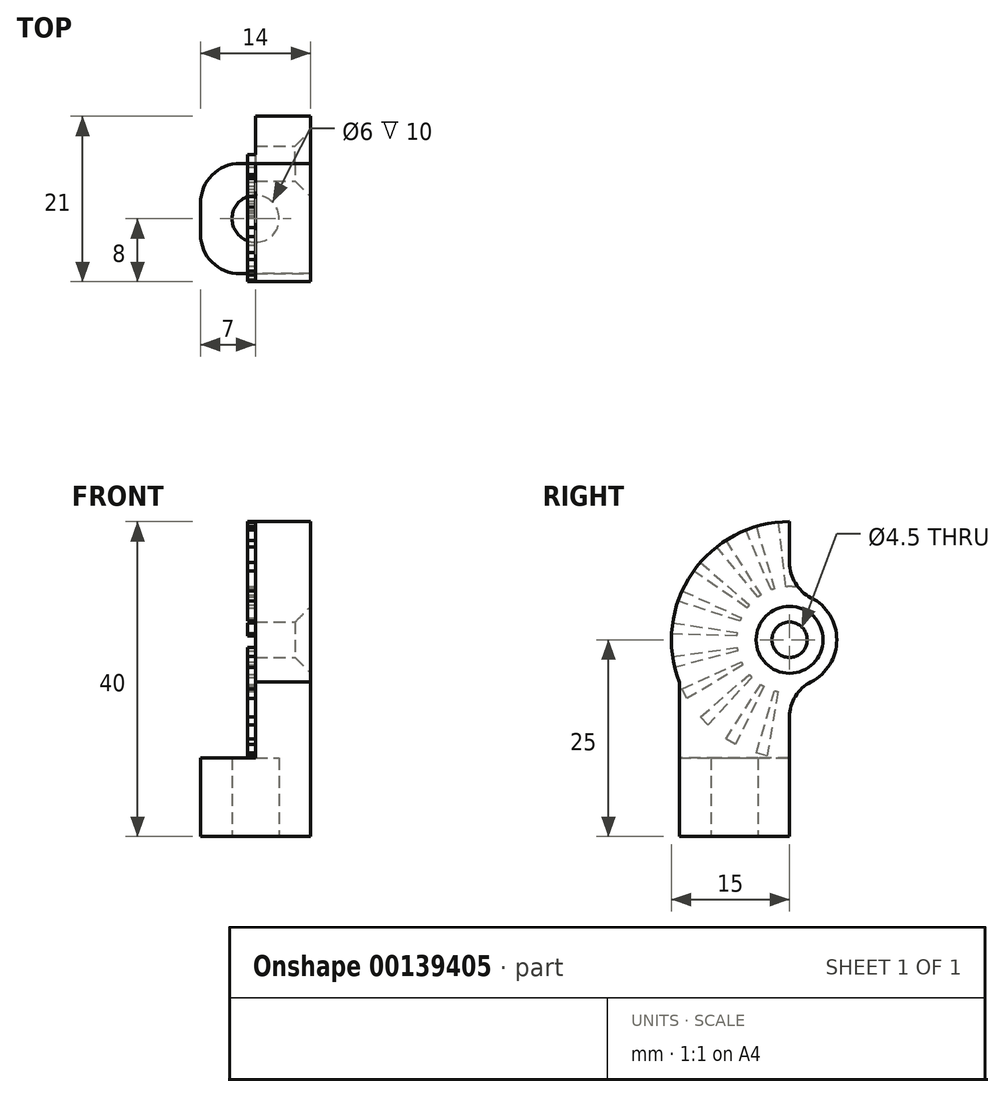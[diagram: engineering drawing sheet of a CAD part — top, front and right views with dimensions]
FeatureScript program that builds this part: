
annotation { "Feature Type Name" : "Feature", "Feature Type Description" : "" }
export const myFeature = defineFeature(function(context is Context, id is Id, definition is map)
    precondition{}
    {
        {
            var Q0;
            Q0=qCreatedBy(makeId("Top.planeOp"),FACE);
            var sketch = newSketch(context, id + "F0", { "sketchPlane" : qUnion([Q0])});
            skLineSegment(sketch, "E0.bottom", {"start": v(7, -7) * mm, "end": v(-7, -7) * mm});
            skLineSegment(sketch, "E0.top", {"start": v(7, 7) * mm, "end": v(-7, 7) * mm});
            skLineSegment(sketch, "E0.left", {"start": v(7, -7) * mm, "end": v(7, 7) * mm});
            skLineSegment(sketch, "E0.right", {"start": v(-7, -7) * mm, "end": v(-7, 7) * mm});
            skPoint(sketch, "E0.middle", {"position": v(0, 0) * mm});
            skCircle(sketch, "E1", {"center": v(0, 0) * mm, "radius": 3 * mm});
            skSolve(sketch);
        }
        {
            var Q0;
            Q0 = qSketchRegion(id + "F0", true);
            var Q1;
            Q1=makeQuery(id+"F0.imprint","IMPRINT",FACE,{"disambiguationData":[TD([[makeQuery(id+"F0.imprint","IMPRINT",EDGE,{"derivedFrom":sQuery(id+"F0.wireOp",EDGE,"E0.bottom")}),-1.0]])]});
            extrude(context, id + "F1", {"entities" : qUnion([Q0, Q1]), "depth" : 10 * mm});
        }
        {
            var Q0;
            Q0=makeQuery(id+"F1.opExtrude","SWEPT_FACE",FACE,{"disambiguationData":[OSD([sQuery(id+"F0.wireOp",EDGE,"E0.left")])]});
            var sketch = newSketch(context, id + "F2", { "sketchPlane" : qUnion([Q0])});
            skPoint(sketch, "E2.centerSnap0", {"position": v(0, 10) * mm});
            skLineSegment(sketch, "E3", {"start": v(7, 10) * mm, "end": v(7, 22.75) * mm, "construction": true});
            skArc(sketch, "E4", {"start": v(7, 40) * mm, "mid": v(-8, 25) * mm, "end": v(7, 10) * mm});
            skLineSegment(sketch, "E5", {"start": v(-7, 10) * mm, "end": v(-7, 19.61) * mm});
            skLineSegment(sketch, "E6", {"start": v(7, 40) * mm, "end": v(7, 27.25) * mm});
            skArc(sketch, "E7", {"start": v(7, 19) * mm, "mid": v(13, 25) * mm, "end": v(7, 31) * mm});
            skCircle(sketch, "E8", {"center": v(7, 25) * mm, "radius": 2.25 * mm});
            skLineSegment(sketch, "E9.trimOffspring", {"start": v(7, 27.25) * mm, "end": v(7, 46.14) * mm, "construction": true});
            skLineSegment(sketch, "E10.trimOffspring", {"start": v(7, 22.75) * mm, "end": v(7, 10) * mm});
            skSolve(sketch);
        }
        {
            var Q0;
            Q0 = qSketchRegion(id + "F2", true);
            var Q1;
            {var subQ1=sQuery(id+"F2.wireOp",EDGE,"E6");var subQ5=sQuery(id+"F2.wireOp",EDGE,"E4");var subQ6=makeQuery(id+"F2.imprint","INTERSECT",VERTEX,{"derivedFrom":[subQ5,subQ1]});Q1=makeQuery(id+"F2.imprint","IMPRINT",FACE,{"disambiguationData":[TD([[makeQuery(id+"F2.imprint","IMPRINT",EDGE,{"disambiguationData":[TD([[subQ6,-1.0]])],"derivedFrom":subQ5}),1.0]])]});}
            var Q2;
            {var subQ3=sQuery(id+"F2.wireOp",EDGE,"E5");Q2=makeQuery(id+"F2.imprint","IMPRINT",FACE,{"disambiguationData":[TD([[makeQuery(id+"F2.imprint","IMPRINT",EDGE,{"derivedFrom":subQ3}),-1.0]])]});}
            extrude(context, id + "F3", {"entities" : qUnion([Q0, Q1, Q2]), "operationType" : NewBodyOperationType.ADD, "oppositeDirection" : true, "depth" : 7 * mm});
        }
        {
            var Q0;
            Q0=makeQuery(id+"F3.opExtrude","CAP_FACE",FACE,{"disambiguationData":[OSD([sQuery(id+"F0.wireOp",EDGE,"E0.left"),sQuery(id+"F2.wireOp",EDGE,"E4"),sQuery(id+"F2.wireOp",EDGE,"E5"),sQuery(id+"F2.wireOp",EDGE,"E6"),sQuery(id+"F2.wireOp",EDGE,"E7"),sQuery(id+"F2.wireOp",EDGE,"E8"),sQuery(id+"F2.wireOp",EDGE,"E10.trimOffspring")])],"isStart":false});
            var sketch = newSketch(context, id + "F4", { "sketchPlane" : qUnion([Q0])});
            skPoint(sketch, "E11.center", {"position": v(0, 0) * mm});
            skArc(sketch, "E12", {"start": v(-7, 18.25) * mm, "mid": v(-0.25, 25) * mm, "end": v(-7, 31.75) * mm, "construction": true});
            skLineSegment(sketch, "E13", {"start": v(-7, 40) * mm, "end": v(-7, 31.75) * mm});
            skLineSegment(sketch, "E14", {"start": v(-7, 31.75) * mm, "end": v(-6.55, 31.73) * mm});
            skLineSegment(sketch, "E15", {"start": v(-6.55, 31.73) * mm, "end": v(-5.6, 39.93) * mm});
            skLineSegment(sketch, "E16", {"start": v(-5.6, 39.93) * mm, "end": v(-7, 40) * mm});
            skLineSegment(sketch, "E17.1.0", {"start": v(-1.45, 38.94) * mm, "end": v(-2.77, 39.4) * mm});
            skLineSegment(sketch, "E17.1.1", {"start": v(-2.77, 39.4) * mm, "end": v(-5.1, 31.48) * mm});
            skLineSegment(sketch, "E17.1.2", {"start": v(-5.1, 31.48) * mm, "end": v(-4.67, 31.34) * mm});
            skLineSegment(sketch, "E17.1.3", {"start": v(-4.67, 31.34) * mm, "end": v(-1.45, 38.94) * mm});
            skLineSegment(sketch, "E17.2.0", {"start": v(2.25, 36.8) * mm, "end": v(1.1, 37.62) * mm});
            skLineSegment(sketch, "E17.2.1", {"start": v(1.1, 37.62) * mm, "end": v(-3.35, 30.68) * mm});
            skLineSegment(sketch, "E17.2.2", {"start": v(-3.35, 30.68) * mm, "end": v(-2.98, 30.42) * mm});
            skLineSegment(sketch, "E17.2.3", {"start": v(-2.98, 30.42) * mm, "end": v(2.25, 36.8) * mm});
            skLineSegment(sketch, "E17.3.0", {"start": v(5.2, 33.72) * mm, "end": v(4.34, 34.82) * mm});
            skLineSegment(sketch, "E17.3.1", {"start": v(4.34, 34.82) * mm, "end": v(-1.9, 29.42) * mm});
            skLineSegment(sketch, "E17.3.2", {"start": v(-1.9, 29.42) * mm, "end": v(-1.62, 29.07) * mm});
            skLineSegment(sketch, "E17.3.3", {"start": v(-1.62, 29.07) * mm, "end": v(5.2, 33.72) * mm});
            skLineSegment(sketch, "E17.4.0", {"start": v(7.17, 29.93) * mm, "end": v(6.64, 31.23) * mm});
            skLineSegment(sketch, "E17.4.1", {"start": v(6.64, 31.23) * mm, "end": v(-0.86, 27.8) * mm});
            skLineSegment(sketch, "E17.4.2", {"start": v(-0.86, 27.8) * mm, "end": v(-0.69, 27.39) * mm});
            skLineSegment(sketch, "E17.4.3", {"start": v(-0.69, 27.39) * mm, "end": v(7.17, 29.93) * mm});
            skLineSegment(sketch, "E17.5.0", {"start": v(7.98, 25.74) * mm, "end": v(7.85, 27.13) * mm});
            skLineSegment(sketch, "E17.5.1", {"start": v(7.85, 27.13) * mm, "end": v(-0.32, 25.96) * mm});
            skLineSegment(sketch, "E17.5.2", {"start": v(-0.32, 25.96) * mm, "end": v(-0.27, 25.51) * mm});
            skLineSegment(sketch, "E17.5.3", {"start": v(-0.27, 25.51) * mm, "end": v(7.98, 25.74) * mm});
            skLineSegment(sketch, "E17.6.0", {"start": v(7.58, 21.5) * mm, "end": v(7.85, 22.87) * mm});
            skLineSegment(sketch, "E17.6.1", {"start": v(7.85, 22.87) * mm, "end": v(-0.32, 24.04) * mm});
            skLineSegment(sketch, "E17.6.2", {"start": v(-0.32, 24.04) * mm, "end": v(-0.4, 23.6) * mm});
            skLineSegment(sketch, "E17.6.3", {"start": v(-0.4, 23.6) * mm, "end": v(7.58, 21.5) * mm});
            skLineSegment(sketch, "E17.7.0", {"start": v(6, 17.52) * mm, "end": v(6.64, 18.77) * mm});
            skLineSegment(sketch, "E17.7.1", {"start": v(6.64, 18.77) * mm, "end": v(-0.86, 22.2) * mm});
            skLineSegment(sketch, "E17.7.2", {"start": v(-0.86, 22.2) * mm, "end": v(-1.06, 21.8) * mm});
            skLineSegment(sketch, "E17.7.3", {"start": v(-1.06, 21.8) * mm, "end": v(6, 17.52) * mm});
            skLineSegment(sketch, "E17.8.0", {"start": v(3.37, 14.16) * mm, "end": v(4.34, 15.18) * mm});
            skLineSegment(sketch, "E17.8.1", {"start": v(4.34, 15.18) * mm, "end": v(-1.9, 20.58) * mm});
            skLineSegment(sketch, "E17.8.2", {"start": v(-1.9, 20.58) * mm, "end": v(-2.2, 20.25) * mm});
            skLineSegment(sketch, "E17.8.3", {"start": v(-2.2, 20.25) * mm, "end": v(3.37, 14.16) * mm});
            skLineSegment(sketch, "E17.9.0", {"start": v(-0.1, 11.68) * mm, "end": v(1.1, 12.38) * mm});
            skLineSegment(sketch, "E17.9.1", {"start": v(1.1, 12.38) * mm, "end": v(-3.35, 19.32) * mm});
            skLineSegment(sketch, "E17.9.2", {"start": v(-3.35, 19.32) * mm, "end": v(-3.74, 19.1) * mm});
            skLineSegment(sketch, "E17.9.3", {"start": v(-3.74, 19.1) * mm, "end": v(-0.1, 11.68) * mm});
            skLineSegment(sketch, "E17.10.0", {"start": v(-4.13, 10.28) * mm, "end": v(-2.77, 10.6) * mm});
            skLineSegment(sketch, "E17.10.1", {"start": v(-2.77, 10.6) * mm, "end": v(-5.1, 18.52) * mm});
            skLineSegment(sketch, "E17.10.2", {"start": v(-5.1, 18.52) * mm, "end": v(-5.53, 18.41) * mm});
            skLineSegment(sketch, "E17.10.3", {"start": v(-5.53, 18.41) * mm, "end": v(-4.13, 10.28) * mm});
            skLineSegment(sketch, "E17.11.0", {"start": v(-8.4, 10.07) * mm, "end": v(-7, 10) * mm});
            skLineSegment(sketch, "E17.11.1", {"start": v(-7, 10) * mm, "end": v(-7, 18.25) * mm});
            skLineSegment(sketch, "E17.11.2", {"start": v(-7, 18.25) * mm, "end": v(-7.45, 18.27) * mm});
            skLineSegment(sketch, "E17.11.3", {"start": v(-7.45, 18.27) * mm, "end": v(-8.4, 10.07) * mm});
            skLineSegment(sketch, "E17.anchor1", {"start": v(-7, 25) * mm, "end": v(-7, 40) * mm, "construction": true});
            skLineSegment(sketch, "E17.anchor2", {"start": v(-7, 25) * mm, "end": v(-7, 10) * mm, "construction": true});
            skArc(sketch, "E18", {"start": v(-7, 18.25) * mm, "mid": v(-0.25, 25) * mm, "end": v(-7, 31.75) * mm});
            skSolve(sketch);
        }
        {
            var Q0;
            {var subQ0=sQuery(id+"F4.wireOp",EDGE,"E13");Q0=makeQuery(id+"F4.imprint","IMPRINT",FACE,{"disambiguationData":[TD([[makeQuery(id+"F4.imprint","IMPRINT",EDGE,{"derivedFrom":subQ0}),1.0]])]});}
            var Q1;
            Q1=makeQuery(id+"F4.imprint","IMPRINT",FACE,{"disambiguationData":[TD([[makeQuery(id+"F4.imprint","IMPRINT",EDGE,{"derivedFrom":sQuery(id+"F4.wireOp",EDGE,"E17.1.0")}),1.0]])]});
            var Q2;
            Q2=makeQuery(id+"F4.imprint","IMPRINT",FACE,{"disambiguationData":[TD([[makeQuery(id+"F4.imprint","IMPRINT",EDGE,{"derivedFrom":sQuery(id+"F4.wireOp",EDGE,"E17.2.0")}),1.0]])]});
            var Q3;
            Q3=makeQuery(id+"F4.imprint","IMPRINT",FACE,{"disambiguationData":[TD([[makeQuery(id+"F4.imprint","IMPRINT",EDGE,{"derivedFrom":sQuery(id+"F4.wireOp",EDGE,"E17.3.0")}),1.0]])]});
            var Q4;
            Q4=makeQuery(id+"F4.imprint","IMPRINT",FACE,{"disambiguationData":[TD([[makeQuery(id+"F4.imprint","IMPRINT",EDGE,{"derivedFrom":sQuery(id+"F4.wireOp",EDGE,"E17.4.0")}),1.0]])]});
            var Q5;
            Q5=makeQuery(id+"F4.imprint","IMPRINT",FACE,{"disambiguationData":[TD([[makeQuery(id+"F4.imprint","IMPRINT",EDGE,{"derivedFrom":sQuery(id+"F4.wireOp",EDGE,"E17.5.0")}),1.0]])]});
            var Q6;
            Q6=makeQuery(id+"F4.imprint","IMPRINT",FACE,{"disambiguationData":[TD([[makeQuery(id+"F4.imprint","IMPRINT",EDGE,{"derivedFrom":sQuery(id+"F4.wireOp",EDGE,"E17.6.0")}),1.0]])]});
            var Q7;
            Q7=makeQuery(id+"F4.imprint","IMPRINT",FACE,{"disambiguationData":[TD([[makeQuery(id+"F4.imprint","IMPRINT",EDGE,{"derivedFrom":sQuery(id+"F4.wireOp",EDGE,"E17.7.0")}),1.0]])]});
            var Q8;
            Q8=makeQuery(id+"F4.imprint","IMPRINT",FACE,{"disambiguationData":[TD([[makeQuery(id+"F4.imprint","IMPRINT",EDGE,{"derivedFrom":sQuery(id+"F4.wireOp",EDGE,"E17.8.0")}),1.0]])]});
            var Q9;
            Q9=makeQuery(id+"F4.imprint","IMPRINT",FACE,{"disambiguationData":[TD([[makeQuery(id+"F4.imprint","IMPRINT",EDGE,{"derivedFrom":sQuery(id+"F4.wireOp",EDGE,"E17.9.0")}),1.0]])]});
            var Q10;
            Q10=makeQuery(id+"F4.imprint","IMPRINT",FACE,{"disambiguationData":[TD([[makeQuery(id+"F4.imprint","IMPRINT",EDGE,{"derivedFrom":sQuery(id+"F4.wireOp",EDGE,"E17.10.0")}),1.0]])]});
            extrude(context, id + "F5", {"entities" : qUnion([Q0, Q1, Q2, Q3, Q4, Q5, Q6, Q7, Q8, Q9, Q10]), "operationType" : NewBodyOperationType.ADD, "depth" : 1 * mm});
        }
        {
            var Q0;
            Q0=makeQuery(id+"F3.opExtrude","SWEPT_EDGE",EDGE,{"disambiguationData":[OSD([sQuery(id+"F2.wireOp",EDGE,"E6"),sQuery(id+"F2.wireOp",EDGE,"E7")])]});
            var Q1;
            Q1=makeQuery(id+"F3.opExtrude","SWEPT_EDGE",EDGE,{"disambiguationData":[OSD([sQuery(id+"F2.wireOp",EDGE,"E7"),sQuery(id+"F2.wireOp",EDGE,"E10.trimOffspring")])]});
            fillet(context, id + "F6", {"entities" : qUnion([Q0, Q1]), "radius" : 5 * mm, "tangentPropagation" : true, "allowEdgeOverflow" : false});
        }
        {
            var Q0;
            Q0=makeQuery(id+"F1.opExtrude","SWEPT_EDGE",EDGE,{"disambiguationData":[OSD([sQuery(id+"F0.wireOp",EDGE,"E0.top"),sQuery(id+"F0.wireOp",EDGE,"E0.right")])]});
            var Q1;
            Q1=makeQuery(id+"F1.opExtrude","SWEPT_EDGE",EDGE,{"disambiguationData":[OSD([sQuery(id+"F0.wireOp",EDGE,"E0.bottom"),sQuery(id+"F0.wireOp",EDGE,"E0.right")])]});
            fillet(context, id + "F7", {"entities" : qUnion([Q0, Q1]), "radius" : 5 * mm, "tangentPropagation" : true, "allowEdgeOverflow" : false});
        }
        {
            var Q0;
            Q0=makeQuery(id+"F3.opExtrude","CAP_EDGE",EDGE,{"disambiguationData":[OSD([sQuery(id+"F2.wireOp",EDGE,"E8")])],"isStart":true});
            chamfer(context, id + "F8", {"entities" : qUnion([Q0]), "width" : 2 * mm, "tangentPropagation" : true});
        }
    });
